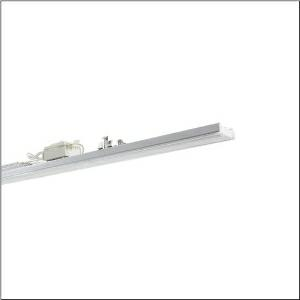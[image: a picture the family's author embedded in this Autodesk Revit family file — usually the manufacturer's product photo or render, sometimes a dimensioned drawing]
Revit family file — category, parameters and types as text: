
# Revit family: licross_r__11_recessed_mo_51tl19de445g_400a
name_source: partatom
category: Lighting Fixtures
units: mm (PartAtom-declared; Revit-internal decimal feet)

## family parameters
Cut with Voids When Loaded = No
Host = Face
Light Source = No
Part Type = Normal
Room Calculation Point = No
Round Connector Dimension = Use Diameter
Shared = No

## types (1)
- --- (1 x LED, 4900 lm, 29.6 W, 4000K)
    Apparent Load = 30 VA
    CIE Flux Codes = 55 90 98 100 100
    Color Rendering = 80
    Color Temperature = 4000K
    Default Elevation = 1800 mm
    Description = Licross® 11 Recessed MO, luminaire insert, of sheet steel, coil coated, white, length: 750mm, width: 66mm, height: 67mm, LED rated luminous flux: 4.910lm, light colour: 840, control gear: DALI 2, with plug, 5-pole, with phase selection, mains connection: 220..240V, AC, 50/60Hz, rated input power: 30W, internal wiring halogen-free, primary light control with lens, of plastic, primary optical cover: cover, of PMMA, light emission: direct distribution, primary light characteristic: double asymmetric, protection rating (complete): IP40, insulation class (complete): insulation class I (protective earthing), certification: CE, ENEC, VDE, UKCA, protection symbol: D if used in an environment without relevant dust loads with corresponding accessories, impact resistance: IK06, permissible ambient temperature for indoor applications: -25..+35°C, corresponds to IFS (International Featured Standards) requirements for safety and quality in the food industry, reducing of maximum allowable ambient temperature of 5°C with ceiling mounting, LABS conformity tested according to VDMA 24364:2018-05, packaging unit: 1 piece
    Height = 58 mm
    Lamp = 1 x LED
    Lamp Light Flux = 4900 lm
    Lamp Power = 29.6 W
    Lamp count = 1
    Length = 750 mm
    Luminous efficacy = 166 lm/W
    Manufacturer = Siteco
    ModVariant = No
    Model = 51TL19DE445G
    Mounting Place = Ceiling
    Mounting Type = Pendant
    Number of Poles = 1
    OnlyDefault = Yes
    Power Factor = 1
    Product Name = Licross® 11 Recessed MO
    Product group = luminaire insert | ceiling pendant
    ProductGroupID = 902
    Protection Class = Protection class I
    Protection Degree = IP 40
    RLX_Detail_Level = 1
    RLX_Emergency_Light_Flux = 0 lm
    RLX_Emergency_Type = 0
    RLX_Emergency_Type_DB = No
    RlxData = <blob elided: 29329 chars, md5=df9d4316>
    Socket = socket
    Standby Power = 0 W
    System Light Flux = 4900 lm
    System Power = 30 W
    Type Comments = factory setting: luminous flux: 100 % | dim-lin: 254 | 378 mA
    Type Image = l_1296930.jpg
    URL = http://relux.com
    VarID = @adj_122073
    Voltage = 0 V
    Weight = 0.00 kg
    Width = 66 mm

## geometry (parser evidence)
native form markers: Blend x4, Sweep x9
no freeform markers — native parametric forms only
